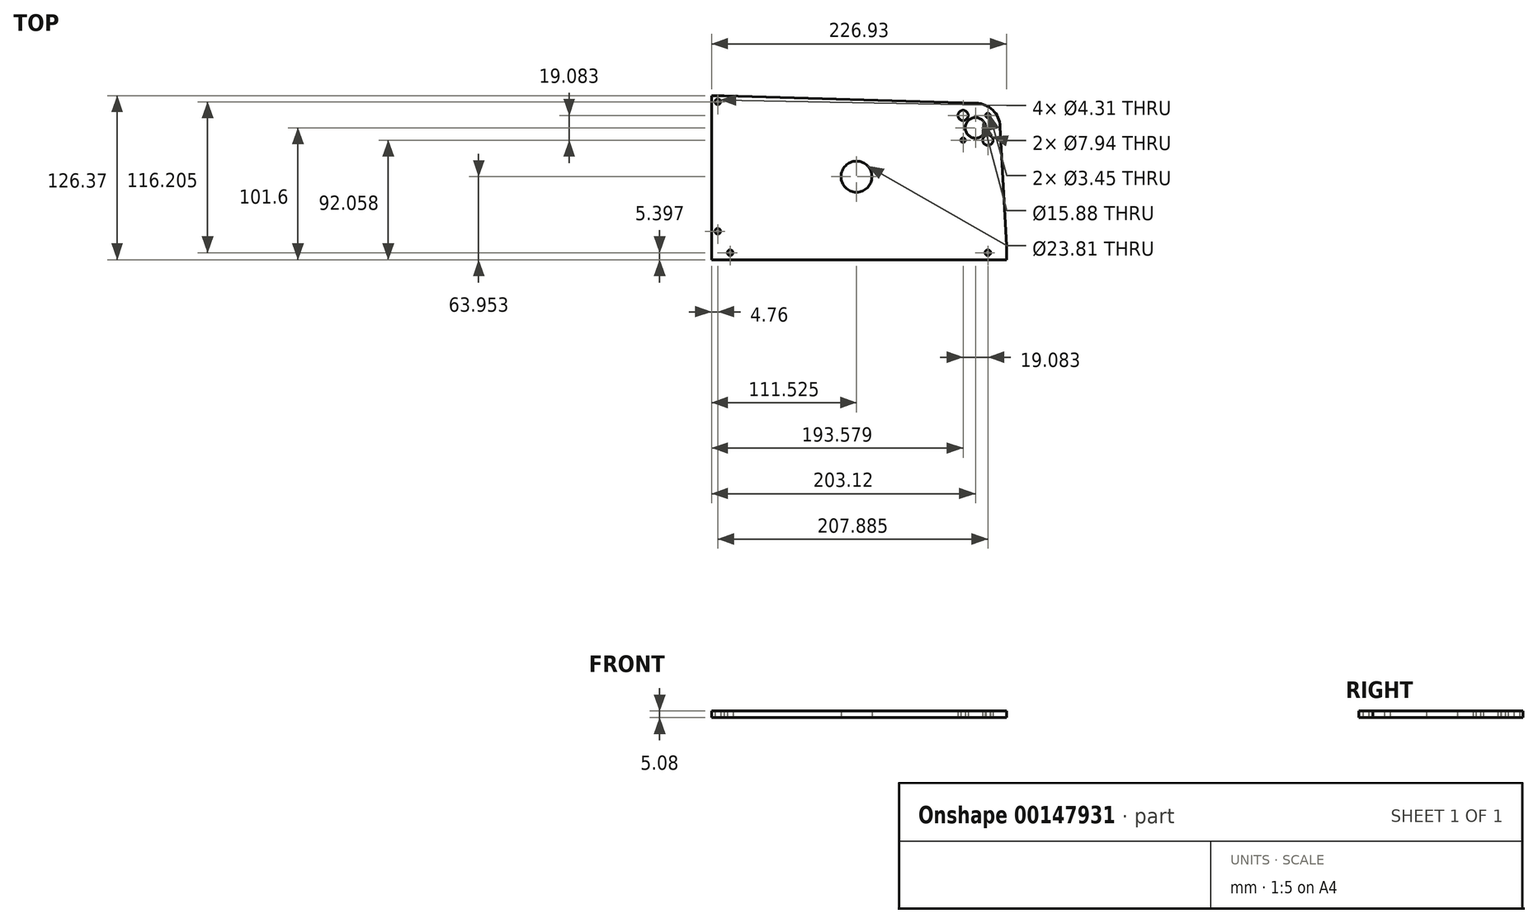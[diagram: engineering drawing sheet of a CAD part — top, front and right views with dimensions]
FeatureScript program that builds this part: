
annotation { "Feature Type Name" : "Feature", "Feature Type Description" : "" }
export const myFeature = defineFeature(function(context is Context, id is Id, definition is map)
    precondition{}
    {
        {
            var Q0;
            Q0=qCreatedBy(makeId("Top.planeOp"),FACE);
            var sketch = newSketch(context, id + "F0", { "sketchPlane" : qUnion([Q0])});
            skCircle(sketch, "E0", {"center": v(0, 0) * mm, "radius": 7.94 * mm});
            skCircle(sketch, "E1", {"center": v(-9.54, 9.54) * mm, "radius": 5.56 * mm, "construction": true});
            skCircle(sketch, "E2", {"center": v(-9.54, 9.54) * mm, "radius": 3.97 * mm});
            skCircle(sketch, "E3", {"center": v(9.54, -9.54) * mm, "radius": 3.97 * mm});
            skLineSegment(sketch, "E4.bottom", {"start": v(-193.6, 24.76) * mm, "end": v(0.56, 19.04) * mm});
            skLineSegment(sketch, "E4.top", {"start": v(-203.12, -101.6) * mm, "end": v(23.81, -101.6) * mm});
            skLineSegment(sketch, "E4.left", {"start": v(-203.12, 24.76) * mm, "end": v(-203.12, -101.6) * mm});
            skLineSegment(sketch, "E5.bottom", {"start": v(-9.54, 9.54) * mm, "end": v(9.54, 9.54) * mm, "construction": true});
            skLineSegment(sketch, "E5.top", {"start": v(-9.54, -9.54) * mm, "end": v(9.54, -9.54) * mm, "construction": true});
            skLineSegment(sketch, "E5.left", {"start": v(-9.54, 9.54) * mm, "end": v(-9.54, -9.54) * mm, "construction": true});
            skLineSegment(sketch, "E5.right", {"start": v(9.54, 9.54) * mm, "end": v(9.54, -9.54) * mm, "construction": true});
            skCircle(sketch, "E6", {"center": v(-9.54, -9.54) * mm, "radius": 1.73 * mm});
            skCircle(sketch, "E7", {"center": v(9.54, 9.54) * mm, "radius": 1.73 * mm});
            skArc(sketch, "E8", {"start": v(19.02, 1) * mm, "mid": v(13.32, 13.62) * mm, "end": v(0.56, 19.04) * mm});
            skLineSegment(sketch, "E9", {"start": v(23.81, -101.6) * mm, "end": v(23.81, -90.8) * mm});
            skLineSegment(sketch, "E10", {"start": v(23.81, -90.8) * mm, "end": v(19.02, 1) * mm});
            skLineSegment(sketch, "E11", {"start": v(0, 0) * mm, "end": v(0, -101.6) * mm, "construction": true});
            skLineSegment(sketch, "E12", {"start": v(23.81, -96.2) * mm, "end": v(9.53, -96.2) * mm, "construction": true});
            skCircle(sketch, "E13", {"center": v(9.53, -96.2) * mm, "radius": 2.15 * mm});
            skLineSegment(sketch, "E14", {"start": v(23.81, -90.8) * mm, "end": v(0, -90.8) * mm, "construction": true});
            skLineSegment(sketch, "E15", {"start": v(-203.12, -96.2) * mm, "end": v(-188.83, -96.2) * mm, "construction": true});
            skCircle(sketch, "E16", {"center": v(-188.83, -96.2) * mm, "radius": 2.15 * mm});
            skLineSegment(sketch, "E17", {"start": v(-198.36, 24.76) * mm, "end": v(-198.36, 20) * mm, "construction": true});
            skLineSegment(sketch, "E18", {"start": v(-198.36, 20) * mm, "end": v(-203.12, 20) * mm, "construction": true});
            skLineSegment(sketch, "E19", {"start": v(-198.36, 20) * mm, "end": v(-198.36, -79.7) * mm, "construction": true});
            skLineSegment(sketch, "E20", {"start": v(-198.36, -79.7) * mm, "end": v(-198.36, -96.2) * mm, "construction": true});
            skCircle(sketch, "E21", {"center": v(-198.36, -79.7) * mm, "radius": 2.15 * mm});
            skCircle(sketch, "E22", {"center": v(-198.36, 20) * mm, "radius": 2.15 * mm});
            skCircle(sketch, "E23", {"center": v(-91.6, -37.65) * mm, "radius": 11.9 * mm});
            skLineSegment(sketch, "E24", {"start": v(-203.12, 24.76) * mm, "end": v(-193.6, 24.76) * mm});
            skSolve(sketch);
        }
        {
            var Q0;
            Q0=qSketchRegion(id+"F0",true);
            extrude(context, id + "F1", {"entities" : qUnion([Q0]), "depth" : 5.08 * mm});
        }
    });
